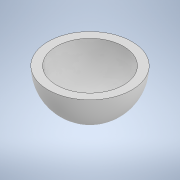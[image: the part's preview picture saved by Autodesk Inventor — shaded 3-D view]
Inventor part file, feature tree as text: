
AUTODESK INVENTOR PART (.ipt)
format: ipt  version: 2022 (Build 260153000, 153)  size: 150,528 bytes
history: native  units: in
note: dims shown in document units (in); Inventor stores cm internally (conversion verified against a paired STEP export)
features: revolve x1, thicken_offset x1, shell x1, sketch x1
ambient origin geometry x8: Origin, YZ Plane, XZ Plane, XY Plane, X Axis, Y Axis, Z Axis, Center Point
bodies: Solid1 (feature_tree)
feature tree (4):
  revolve  "Revolution1"  [1 undecoded]
  thicken_offset  "Thicken1"
  shell  "Shell2"  Thickness=0.25in
  sketch  "Sketch1"  dims[d3=90.0deg d5=0.26in d6=0.25in d7=0.25in d4=0.0344in]
note: 1 required parameter value undecoded (feature->parameter linkage not recoverable at this tier; creation-order binding heuristic only, values carry confidence <= 0.55)
